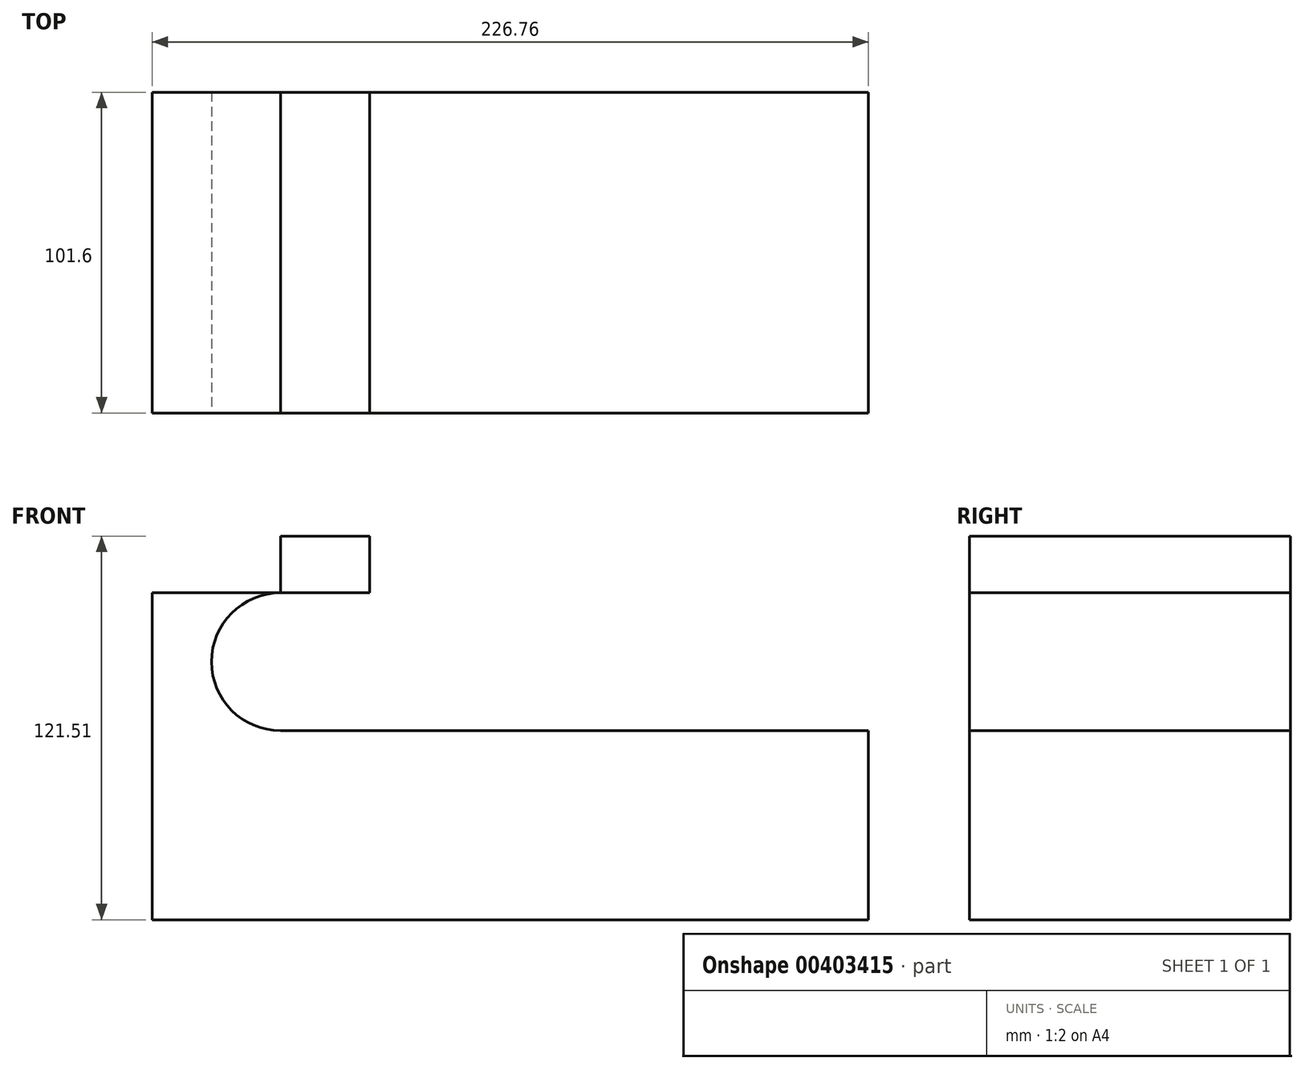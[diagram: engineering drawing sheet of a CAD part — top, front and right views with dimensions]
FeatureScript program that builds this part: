
annotation { "Feature Type Name" : "Feature", "Feature Type Description" : "" }
export const myFeature = defineFeature(function(context is Context, id is Id, definition is map)
    precondition{}
    {
        {
            var Q0;
            Q0=qCreatedBy(makeId("Front.planeOp"),FACE);
            var sketch = newSketch(context, id + "F0", { "sketchPlane" : qUnion([Q0])});
            skLineSegment(sketch, "E0.bottom", {"start": v(-113.38, 29.95) * mm, "end": v(113.38, 29.95) * mm});
            skLineSegment(sketch, "E0.left", {"start": v(-113.38, 29.95) * mm, "end": v(-113.38, -29.95) * mm});
            skLineSegment(sketch, "E0.right", {"start": v(113.38, 29.95) * mm, "end": v(113.38, -29.95) * mm});
            skPoint(sketch, "E0.middle", {"position": v(0, 0) * mm});
            skLineSegment(sketch, "E1.bottom", {"start": v(-113.38, -29.95) * mm, "end": v(-72.74, -29.95) * mm});
            skLineSegment(sketch, "E1.top", {"start": v(-113.38, 91.56) * mm, "end": v(-72.74, 91.56) * mm});
            skLineSegment(sketch, "E1.left", {"start": v(-113.38, -29.95) * mm, "end": v(-113.38, 91.56) * mm});
            skLineSegment(sketch, "E1.right", {"start": v(-72.74, -29.95) * mm, "end": v(-72.74, 91.56) * mm});
            skLineSegment(sketch, "E2.bottom", {"start": v(-113.38, 91.56) * mm, "end": v(-44.5, 91.56) * mm});
            skLineSegment(sketch, "E2.top", {"start": v(-113.38, 73.6) * mm, "end": v(-44.5, 73.6) * mm});
            skLineSegment(sketch, "E2.left", {"start": v(-113.38, 91.56) * mm, "end": v(-113.38, 73.6) * mm});
            skLineSegment(sketch, "E2.right", {"start": v(-44.5, 91.56) * mm, "end": v(-44.5, 73.6) * mm});
            skLineSegment(sketch, "E3", {"start": v(-72.74, -29.95) * mm, "end": v(113.38, -29.95) * mm});
            skLineSegment(sketch, "E4.bottom", {"start": v(113.38, 29.95) * mm, "end": v(88.9, 29.95) * mm});
            skLineSegment(sketch, "E4.top", {"start": v(113.38, 164.98) * mm, "end": v(88.9, 164.98) * mm});
            skLineSegment(sketch, "E4.left", {"start": v(113.38, 29.95) * mm, "end": v(113.38, 164.98) * mm});
            skLineSegment(sketch, "E4.right", {"start": v(88.9, 29.95) * mm, "end": v(88.9, 164.98) * mm});
            skLineSegment(sketch, "E5.bottom", {"start": v(0, 29.95) * mm, "end": v(38.1, 29.95) * mm});
            skLineSegment(sketch, "E5.top", {"start": v(0, 164.98) * mm, "end": v(38.1, 164.98) * mm});
            skLineSegment(sketch, "E5.left", {"start": v(0, 29.95) * mm, "end": v(0, 164.98) * mm});
            skLineSegment(sketch, "E5.right", {"start": v(38.1, 29.95) * mm, "end": v(38.1, 164.98) * mm});
            skSolve(sketch);
        }
        {
            var Q0;
            Q0=makeQuery(id+"F0.imprint","IMPRINT",FACE,{"disambiguationData":[TD([[makeQuery(id+"F0.imprint","IMPRINT",EDGE,{"derivedFrom":sQuery(id+"F0.wireOp",EDGE,"E4.bottom")}),-1.0]])]});
            var Q1;
            Q1=makeQuery(id+"F0.imprint","IMPRINT",FACE,{"disambiguationData":[TD([[makeQuery(id+"F0.imprint","IMPRINT",EDGE,{"derivedFrom":sQuery(id+"F0.wireOp",EDGE,"E5.bottom")}),1.0]])]});
            var Q2;
            Q2=makeQuery(id+"F0.imprint","IMPRINT",FACE,{"disambiguationData":[TD([[makeQuery(id+"F0.imprint","IMPRINT",EDGE,{"derivedFrom":sQuery(id+"F0.wireOp",EDGE,"E0.right")}),-1.0]])]});
            var Q3;
            {var subQ5=sQuery(id+"F0.wireOp",EDGE,"E1.bottom");Q3=makeQuery(id+"F0.imprint","IMPRINT",FACE,{"disambiguationData":[TD([[makeQuery(id+"F0.imprint","IMPRINT",EDGE,{"derivedFrom":subQ5}),1.0]])]});}
            var Q4;
            {var subQ0=sQuery(id+"F0.wireOp",EDGE,"E1.left");var subQ1=sQuery(id+"F0.wireOp",EDGE,"E0.bottom");var subQ2=makeQuery(id+"F0.imprint","INTERSECT",VERTEX,{"derivedFrom":[subQ1,subQ0]});Q4=makeQuery(id+"F0.imprint","IMPRINT",FACE,{"disambiguationData":[TD([[makeQuery(id+"F0.imprint","IMPRINT",EDGE,{"disambiguationData":[TD([[subQ2,-1.0]])],"derivedFrom":subQ1}),1.0]])]});}
            var Q5;
            {var subQ5=sQuery(id+"F0.wireOp",EDGE,"E2.left");Q5=makeQuery(id+"F0.imprint","IMPRINT",FACE,{"disambiguationData":[TD([[makeQuery(id+"F0.imprint","IMPRINT",EDGE,{"derivedFrom":subQ5}),1.0]])]});}
            var Q6;
            {var subQ5=sQuery(id+"F0.wireOp",EDGE,"E2.right");Q6=makeQuery(id+"F0.imprint","IMPRINT",FACE,{"disambiguationData":[TD([[makeQuery(id+"F0.imprint","IMPRINT",EDGE,{"derivedFrom":subQ5}),-1.0]])]});}
            extrude(context, id + "F1", {"entities" : qUnion([Q0, Q1, Q2, Q3, Q4, Q5, Q6]), "endBound" : BoundingType.SYMMETRIC, "depth" : 101.6 * mm});
        }
        {
            var Q0;
            Q0=makeQuery(id+"F1.opExtrude","CAP_FACE",FACE,{"disambiguationData":[OSD([sQuery(id+"F0.wireOp",EDGE,"E0.bottom"),sQuery(id+"F0.wireOp",EDGE,"E0.right"),sQuery(id+"F0.wireOp",EDGE,"E1.bottom"),sQuery(id+"F0.wireOp",EDGE,"E1.left"),sQuery(id+"F0.wireOp",EDGE,"E1.right"),sQuery(id+"F0.wireOp",EDGE,"E2.bottom"),sQuery(id+"F0.wireOp",EDGE,"E2.top"),sQuery(id+"F0.wireOp",EDGE,"E2.left"),sQuery(id+"F0.wireOp",EDGE,"E2.right"),sQuery(id+"F0.wireOp",EDGE,"E3"),sQuery(id+"F0.wireOp",EDGE,"E4.top"),sQuery(id+"F0.wireOp",EDGE,"E4.left"),sQuery(id+"F0.wireOp",EDGE,"E4.right"),sQuery(id+"F0.wireOp",EDGE,"E5.top"),sQuery(id+"F0.wireOp",EDGE,"E5.left"),sQuery(id+"F0.wireOp",EDGE,"E5.right")])],"isStart":false});
            var sketch = newSketch(context, id + "F2", { "sketchPlane" : qUnion([Q0])});
            skArc(sketch, "E6", {"start": v(-72.74, 73.6) * mm, "mid": v(-94.56, 51.77) * mm, "end": v(-72.74, 29.95) * mm});
            skSolve(sketch);
        }
        {
            var Q0;
            Q0 = qSketchRegion(id + "F2", true);
            var Q1;
            Q1=makeQuery(id+"F2.imprint","IMPRINT",FACE,{"disambiguationData":[TD([[makeQuery(id+"F2.imprint","IMPRINT",EDGE,{"derivedFrom":sQuery(id+"F2.wireOp",EDGE,"E6")}),1.0]])]});
            extrude(context, id + "F3", {"entities" : qUnion([Q0, Q1]), "operationType" : NewBodyOperationType.REMOVE, "oppositeDirection" : true, "depth" : 176.78 * mm});
        }
    });
